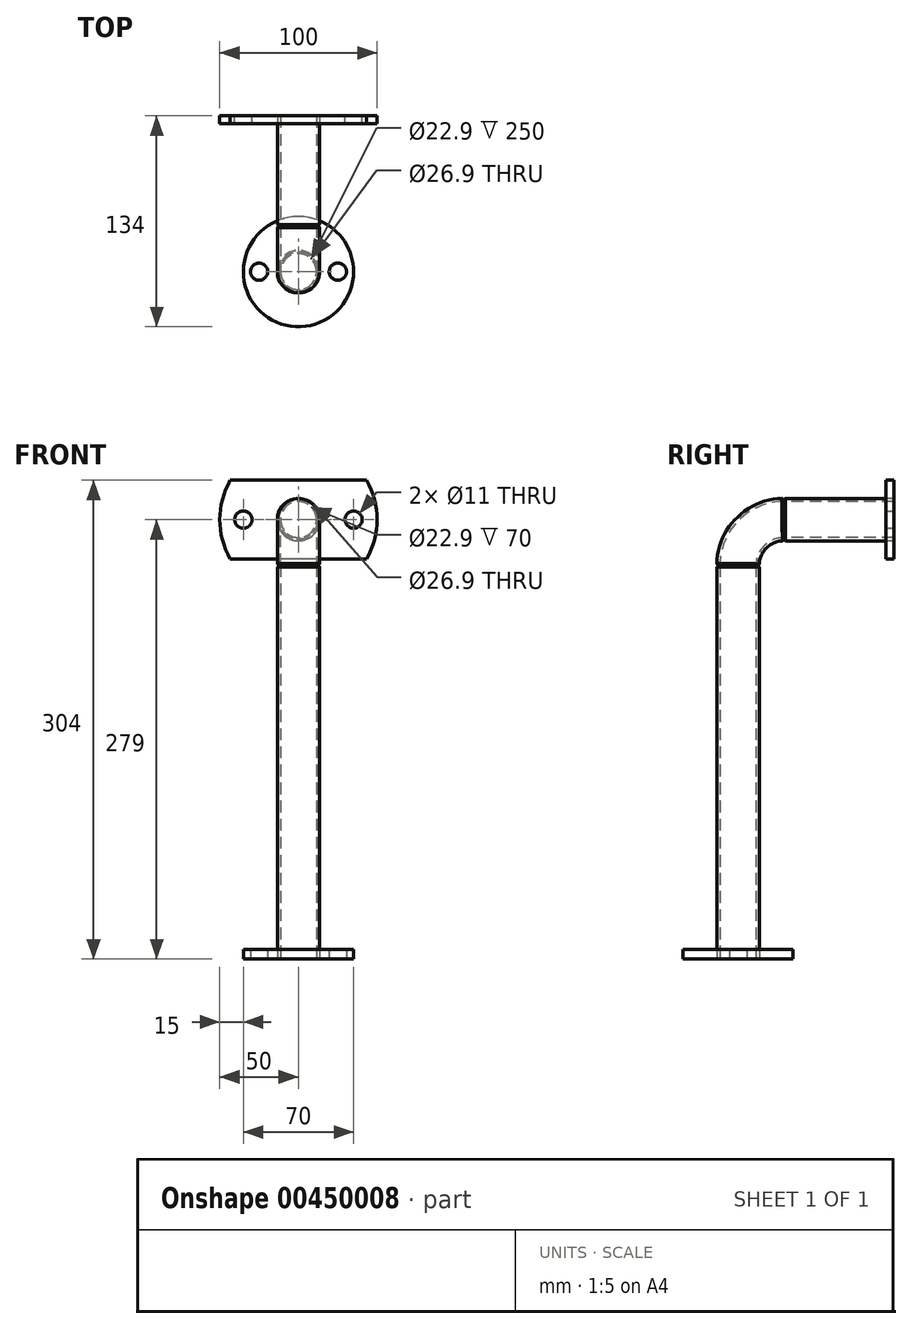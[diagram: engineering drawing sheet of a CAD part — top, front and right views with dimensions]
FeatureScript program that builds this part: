
annotation { "Feature Type Name" : "Feature", "Feature Type Description" : "" }
export const myFeature = defineFeature(function(context is Context, id is Id, definition is map)
    precondition{}
    {
        {
            var Q0;
            Q0=qCreatedBy(makeId("Top.planeOp"),FACE);
            var sketch = newSketch(context, id + "F0", { "sketchPlane" : qUnion([Q0])});
            skCircle(sketch, "E0", {"center": v(0, 0) * mm, "radius": 35 * mm});
            skCircle(sketch, "E1", {"center": v(0, 0) * mm, "radius": 13.45 * mm});
            skCircle(sketch, "E2", {"center": v(25, 0) * mm, "radius": 5.5 * mm});
            skCircle(sketch, "E3.MirrorC", {"center": v(-25, 0) * mm, "radius": 5.5 * mm});
            skCircle(sketch, "E4", {"center": v(0, 0) * mm, "radius": 11.45 * mm});
            skSolve(sketch);
        }
        {
            var Q0;
            Q0=makeQuery(id+"F0.imprint","IMPRINT",FACE,{"disambiguationData":[TD([[makeQuery(id+"F0.imprint","IMPRINT",EDGE,{"derivedFrom":sQuery(id+"F0.wireOp",EDGE,"E0")}),1.0]])]});
            extrude(context, id + "F1", {"entities" : qUnion([Q0]), "depth" : 6 * mm});
        }
        {
            var Q0;
            Q0=makeQuery(id+"F0.imprint","IMPRINT",FACE,{"disambiguationData":[TD([[makeQuery(id+"F0.imprint","IMPRINT",EDGE,{"derivedFrom":sQuery(id+"F0.wireOp",EDGE,"E1")}),1.0]])]});
            extrude(context, id + "F2", {"entities" : qUnion([Q0]), "depth" : 250 * mm});
        }
        {
            var Q0;
            Q0=makeQuery(id+"F2.opExtrude","CAP_FACE",FACE,{"disambiguationData":[OSD([sQuery(id+"F0.wireOp",EDGE,"E1"),sQuery(id+"F0.wireOp",EDGE,"E4")])],"isStart":false});
            var sketch = newSketch(context, id + "F3", { "sketchPlane" : qUnion([Q0])});
            skLineSegment(sketch, "E5", {"start": v(-20, 29) * mm, "end": v(0, 29) * mm});
            skSolve(sketch);
        }
        {
            var Q0;
            Q0=makeQuery(id+"F3.imprint","IMPRINT",FACE,{"disambiguationData":[TD([[makeQuery(id+"F3.imprint","IMPRINT",EDGE,{"derivedFrom":makeQuery(id+"F2.opExtrude","CAP_EDGE",EDGE,{"disambiguationData":[OSD([sQuery(id+"F0.wireOp",EDGE,"E1")])],"isStart":false})}),1.0]])]});
            var Q1;
            Q1=sQuery(id+"F3.wireOp",EDGE,"E5");
            revolve(context, id + "F4", {"entities" : qUnion([Q0]), "axis" : qUnion([Q1]), "revolveType" : RevolveType.ONE_DIRECTION, "oppositeDirection" : true, "angle" : 90 * degree});
        }
        {
            var Q0;
            Q0=makeQuery(id+"F4.opRevolve","CAP_FACE",FACE,{"disambiguationData":[OSD([sQuery(id+"F0.wireOp",EDGE,"E1"),sQuery(id+"F0.wireOp",EDGE,"E4")])],"isStart":false});
            extrude(context, id + "F5", {"entities" : qUnion([Q0]), "depth" : 70 * mm});
        }
        {
            var Q0;
            Q0=makeQuery(id+"F5.opExtrude","CAP_FACE",FACE,{"disambiguationData":[OSD([sQuery(id+"F0.wireOp",EDGE,"E1"),sQuery(id+"F0.wireOp",EDGE,"E4")])],"isStart":false});
            var sketch = newSketch(context, id + "F6", { "sketchPlane" : qUnion([Q0])});
            skLineSegment(sketch, "E6", {"start": v(-43.3, 254) * mm, "end": v(43.3, 254) * mm});
            skArc(sketch, "E7", {"start": v(-43.3, 304) * mm, "mid": v(-50, 279) * mm, "end": v(-43.3, 254) * mm});
            skLineSegment(sketch, "E8", {"start": v(0, 279) * mm, "end": v(0, 304) * mm, "construction": true});
            skArc(sketch, "E9.MirrorCS", {"start": v(43.3, 304) * mm, "mid": v(50, 279) * mm, "end": v(43.3, 254) * mm});
            skLineSegment(sketch, "E10.MirrorCS", {"start": v(-43.3, 304) * mm, "end": v(43.3, 304) * mm});
            skCircle(sketch, "E11", {"center": v(35, 279) * mm, "radius": 5.5 * mm});
            skCircle(sketch, "E12.MirrorC", {"center": v(-35, 279) * mm, "radius": 5.5 * mm});
            skLineSegment(sketch, "E13", {"start": v(0, 279) * mm, "end": v(0, 279) * mm});
            skSolve(sketch);
        }
        {
            var Q0;
            Q0=makeQuery(id+"F6.imprint","IMPRINT",FACE,{"disambiguationData":[TD([[makeQuery(id+"F6.imprint","IMPRINT",EDGE,{"derivedFrom":sQuery(id+"F6.wireOp",EDGE,"E6")}),1.0]])]});
            extrude(context, id + "F7", {"entities" : qUnion([Q0]), "oppositeDirection" : true, "depth" : 5 * mm});
        }
        {
            var Q0;
            Q0=makeQuery(id+"F5.opExtrude","CAP_EDGE",EDGE,{"disambiguationData":[OSD([sQuery(id+"F0.wireOp",EDGE,"E1")])],"isStart":true});
            var Q1;
            Q1=makeQuery(id+"F2.opExtrude","CAP_EDGE",EDGE,{"disambiguationData":[OSD([sQuery(id+"F0.wireOp",EDGE,"E1")])],"isStart":false});
            chamfer(context, id + "F8", {"entities" : qUnion([Q0, Q1]), "width" : 1 * mm, "tangentPropagation" : true});
        }
        {
            var Q0;
            Q0=makeQuery(id+"F4.opRevolve","CAP_EDGE",EDGE,{"disambiguationData":[OSD([sQuery(id+"F0.wireOp",EDGE,"E1")])],"isStart":false});
            var Q1;
            Q1=makeQuery(id+"F4.opRevolve","CAP_EDGE",EDGE,{"disambiguationData":[OSD([sQuery(id+"F0.wireOp",EDGE,"E1")])],"isStart":true});
            chamfer(context, id + "F9", {"entities" : qUnion([Q0, Q1]), "width" : 1 * mm, "tangentPropagation" : true});
        }
    });
